# Revit family: QSC CX-Q 4 Channel Amplifier
name_source: partatom
category: Generic Models
revit_build: Autodesk Revit 2017 (Build: 20190508_0315(x64)
units: mm (PartAtom-declared; Revit-internal decimal feet)

## family parameters
Can host rebar = No
Cut with Voids When Loaded = No
Host = Face
Part Type = Normal
Room Calculation Point = No
Round Connector Dimension = Use Diameter
Shared = No

## types (6) — shared parameters
Depth = 426 mm  [stored 1.39764 ft]
Description = Four-channel Network Amplifier for the Q-SYS Ecosystem
Height = 88.9 mm  [stored 0.291667 ft]
Manufacturer = QSC
Manufacturer URL = http://www.qsc.com
Product Documentation Link = https://www.qsc.com
Product Page URL = https://www.qsc.com
Regulatory Compliance = UL, CE, RoHS/WEEE compliant, FCC Class B (conducted and radiated emissions)
Voltage AC = Universal power supply 100 - 240 VAC, 50 - 60 Hz with active PFC
Width = 482.6 mm  [stored 1.58333 ft]
zero-valued in all types: Default Elevation

## per-type parameters (varying)
| type | Model | Weight Dimensional (kg) | Weight Dimensional (lb) | Weight Product (kg) | Weight Product (lb) |
| CX-Q 2K4 | CX-Q 2k4 | 12.2 | 27 | 10.4 | 23 |
| CX-Qn 2K4 | CX-Qn 2k4 | 12.2 | 27 | 10.4 | 23 |
| CX-Q 4K4 | CX-Q 4k4 | 13.2 | 29 | 11.3 | 25 |
| CX-Qn 4K4 | CX-Qn 4k4 | 13.2 | 29 | 11.3 | 25 |
| CX-Q 8K4 | CX-Q 8K4 | 13.6 | 30 | 11.8 | 26 |
| CX-Qn 8K4 | CX-QN 8K4 | 13.6 | 30 | 11.8 | 26 |

note: [stored X ft] marks values corroborated as IEEE doubles in the binary element streams (Revit-internal decimal feet)

## geometry (parser evidence)
native form markers: Blend x4, Sweep x10
no freeform markers — native parametric forms only
